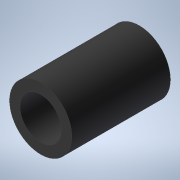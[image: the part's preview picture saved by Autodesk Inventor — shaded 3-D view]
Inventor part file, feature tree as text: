
AUTODESK INVENTOR PART (.ipt)
format: ipt  version: 2021 (Build 250183000, 183)  size: 96,256 bytes
history: native  units: mm
features: extrude x1, sketch x1
ambient origin geometry x8: Origin, YZ Plane, XZ Plane, XY Plane, X Axis, Y Axis, Z Axis, Center Point
bodies: Solid1 (feature_tree)
feature tree (2):
  extrude  "Extrusion1"  Depth=19.0mm
  sketch  "Sketch1"  dims[d0=12.0mm d1=8.0mm d2=19.0mm d3=0.0mm]
